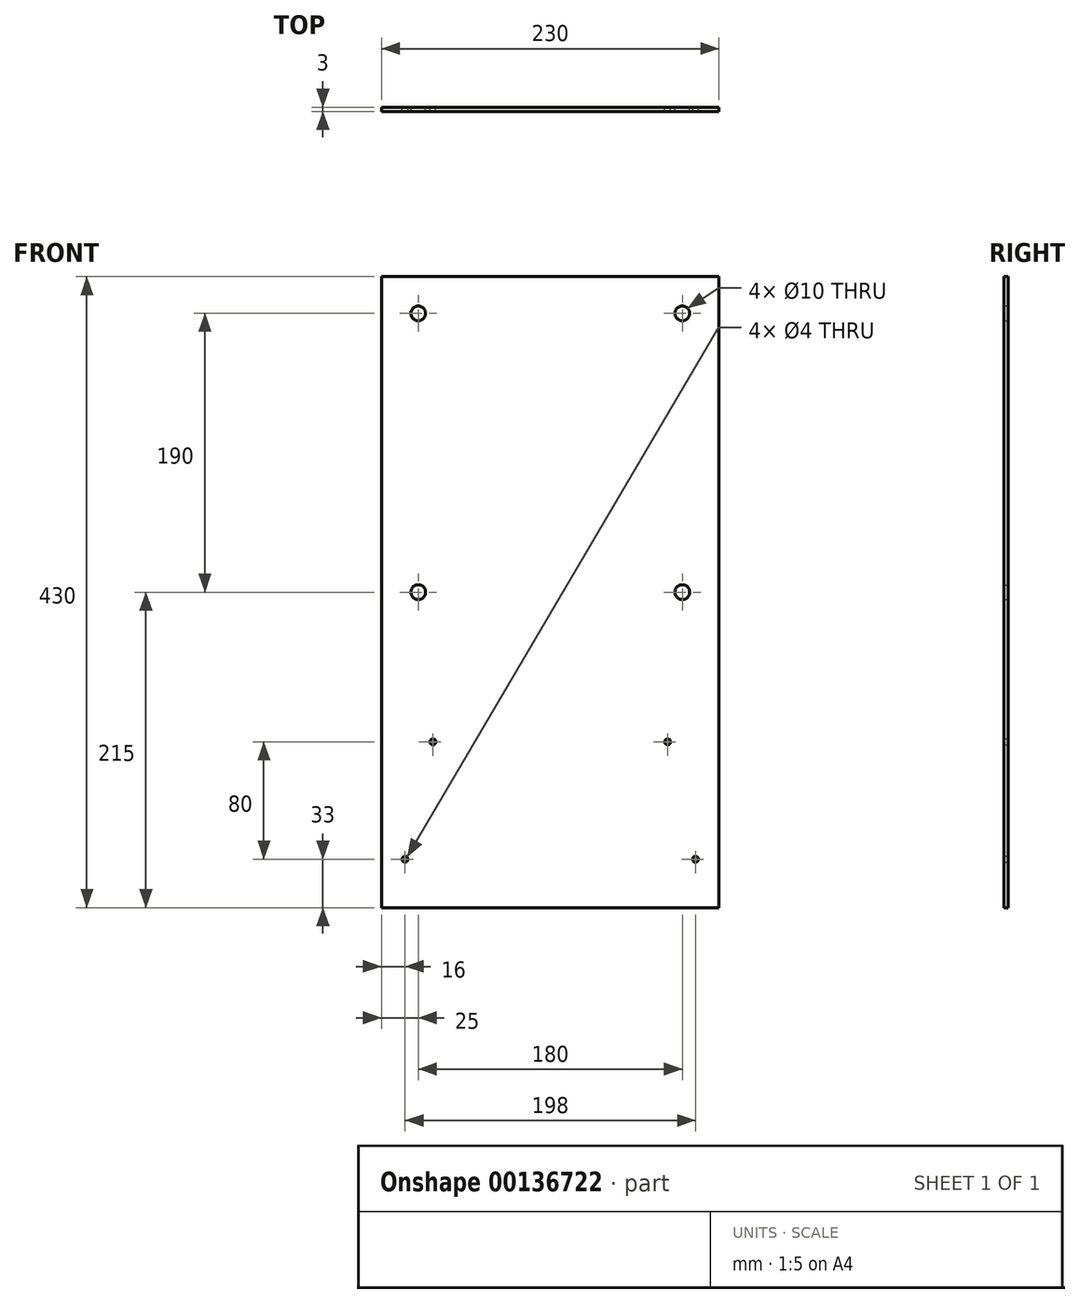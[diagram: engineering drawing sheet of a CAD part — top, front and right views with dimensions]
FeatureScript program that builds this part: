
annotation { "Feature Type Name" : "Feature", "Feature Type Description" : "" }
export const myFeature = defineFeature(function(context is Context, id is Id, definition is map)
    precondition{}
    {
        {
            var Q0;
            Q0=qCreatedBy(makeId("Front.planeOp"),FACE);
            var sketch = newSketch(context, id + "F0", { "sketchPlane" : qUnion([Q0])});
            skLineSegment(sketch, "E0.bottom", {"start": v(-115, -215) * mm, "end": v(115, -215) * mm});
            skLineSegment(sketch, "E0.top", {"start": v(-115, 215) * mm, "end": v(115, 215) * mm});
            skLineSegment(sketch, "E0.left", {"start": v(-115, -215) * mm, "end": v(-115, 215) * mm});
            skLineSegment(sketch, "E0.right", {"start": v(115, -215) * mm, "end": v(115, 215) * mm});
            skPoint(sketch, "E0.middle", {"position": v(0, 0) * mm});
            skLineSegment(sketch, "E1", {"start": v(-115, -215) * mm, "end": v(-115, -182) * mm, "construction": true});
            skPoint(sketch, "E2", {"position": v(-80, -102) * mm});
            skPoint(sketch, "E3", {"position": v(80, -102) * mm});
            skPoint(sketch, "E4", {"position": v(99, -182) * mm});
            skPoint(sketch, "E5", {"position": v(-99, -182) * mm});
            skPoint(sketch, "E6", {"position": v(-90, 190) * mm});
            skPoint(sketch, "E7", {"position": v(90, 190) * mm});
            skPoint(sketch, "E8", {"position": v(90, 0) * mm});
            skPoint(sketch, "E9", {"position": v(-90, 0) * mm});
            skPoint(sketch, "E10.start.orphan", {"position": v(115, 0) * mm});
            skPoint(sketch, "E11.orphan", {"position": v(-115, 0) * mm});
            skCircle(sketch, "E12", {"center": v(-90, 190) * mm, "radius": 5 * mm});
            skCircle(sketch, "E13", {"center": v(90, 190) * mm, "radius": 5 * mm});
            skCircle(sketch, "E14", {"center": v(-80, -102) * mm, "radius": 2 * mm});
            skCircle(sketch, "E15", {"center": v(80, -102) * mm, "radius": 2 * mm});
            skCircle(sketch, "E16", {"center": v(-99, -182) * mm, "radius": 2 * mm});
            skCircle(sketch, "E17", {"center": v(99, -182) * mm, "radius": 2 * mm});
            skCircle(sketch, "E18", {"center": v(-90, 0) * mm, "radius": 5 * mm});
            skCircle(sketch, "E19", {"center": v(90, 0) * mm, "radius": 5 * mm});
            skSolve(sketch);
        }
        {
            var Q0;
            Q0=makeQuery(id+"F0.imprint","IMPRINT",FACE,{"disambiguationData":[TD([[makeQuery(id+"F0.imprint","IMPRINT",EDGE,{"derivedFrom":sQuery(id+"F0.wireOp",EDGE,"E0.bottom")}),1.0]])]});
            extrude(context, id + "F1", {"entities" : qUnion([Q0]), "depth" : 3 * mm});
        }
    });
